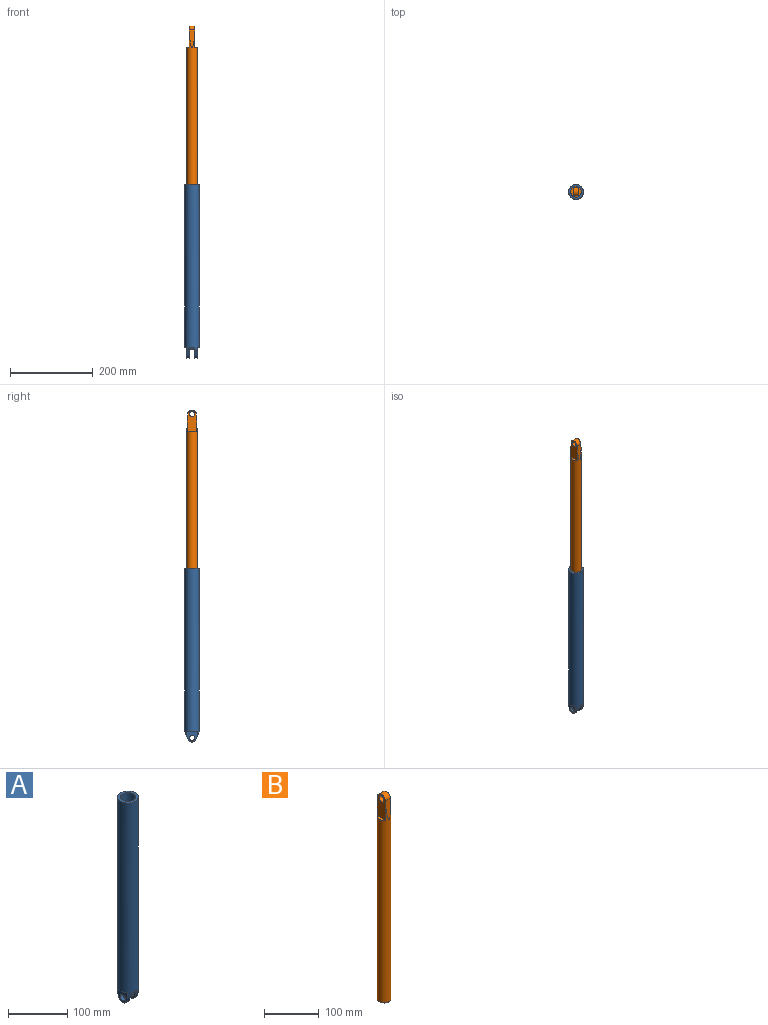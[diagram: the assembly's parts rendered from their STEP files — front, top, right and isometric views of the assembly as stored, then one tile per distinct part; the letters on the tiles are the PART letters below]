
ASSEMBLY  parts=2 mates=1
PART A: 17 faces, bbox 35.6x35.6x419.8 mm
  f0: cylinder r=10.16mm len=18.71mm, axis (-1,0,0), area 151mm2, adj f2,f3,f4,f15
  f1: cylinder r=6.35mm len=12.7mm, axis (-1,0,0), area 253.4mm2, adj f4,f15
  f2: plane 25.4x19.9mm, normal (0,-0.92,-0.39), area 229.3mm2, adj f0,f4,f5,f8,f12,f14,f15,f16
  f3: plane 25.4x19.9mm, normal (0,0.92,-0.39), area 229.3mm2, adj f0,f4,f5,f8,f12,f14,f15,f16
  f4: plane 26.1x24.89mm, normal (-1,0,0), area 429.7mm2, adj f0,f1,f2,f3,f6,f8
  f5: plane 26.1x24.89mm, normal (1,0,0), area 429.7mm2, adj f2,f3,f8,f11,f12,f13
  f6: plane 24.89x5.08mm, normal (0,0,-1), area 87mm2, adj f4,f8
  f7: cylinder r=12.7mm len=381mm, axis (0,0,-1), area 30402.4mm2, adj f9,f10
  f8: cylinder r=17.78mm len=406.3mm, axis (0,0,-1), area 44225.1mm2, adj f2,f3,f4,f5,f6,f9,f11
  f9: plane 35.56x35.56mm, normal (0,0,1), area 486.4mm2, adj f7,f8
  f10: plane 25.4x25.4mm, normal (0,0,1), area 506.7mm2, adj f7
  f11: plane 24.89x5.08mm, normal (0,0,-1), area 87mm2, adj f5,f8
  f12: cylinder r=10.16mm len=18.71mm, axis (-1,0,0), area 151mm2, adj f2,f3,f5,f16
  f13: cylinder r=6.35mm len=12.7mm, axis (-1,0,0), area 253.4mm2, adj f5,f16
  f14: plane 31.71x12.7mm, normal (0,0,-1), area 402.7mm2, adj f2,f3,f15,f16
  f15: plane 31.71x21.54mm, normal (1,0,0), area 343.9mm2, adj f0,f1,f2,f3,f14
  f16: plane 31.71x21.54mm, normal (-1,0,0), area 343.9mm2, adj f2,f3,f12,f13,f14
PART B: 10 faces, bbox 25.4x25.4x459 mm
  f0: plane 43.09x12.7mm, normal (0,-1,0.06), area 430.1mm2, adj f2,f3,f5,f8
  f1: plane 43.09x12.7mm, normal (0,1,0.06), area 430.1mm2, adj f2,f3,f5,f8
  f2: plane 52.64x22mm, normal (1,0,0), area 958.7mm2, adj f0,f1,f5,f6,f8,f9
  f3: plane 52.64x22mm, normal (-1,0,0), area 958.7mm2, adj f0,f1,f4,f5,f8,f9
  f4: plane 22x6.35mm, normal (0,0,1), area 99.1mm2, adj f3,f5
  f5: cylinder r=12.7mm len=435.06mm, axis (0,0,-1), area 32685.7mm2, adj f0,f1,f2,f3,f4,f6,f7
  f6: plane 22x6.35mm, normal (0,0,1), area 99.1mm2, adj f2,f5
  f7: plane 25.4x25.4mm, normal (0,0,-1), area 506.7mm2, adj f5
  f8: cylinder r=10.16mm len=20.28mm, axis (-1,0,0), area 390.1mm2, adj f0,f1,f2,f3
  f9: cylinder r=6.35mm len=12.7mm, axis (-1,0,0), area 506.7mm2, adj f2,f3
PLACE A t=(-245.81,-127.8,141.51)mm fixed
PLACE B t=(-245.81,-127.8,446.31)mm
MATE slider B.f5 <-> A.f7  axis (0,0,-1) through (-245.81,-127.8,446.31)mm
